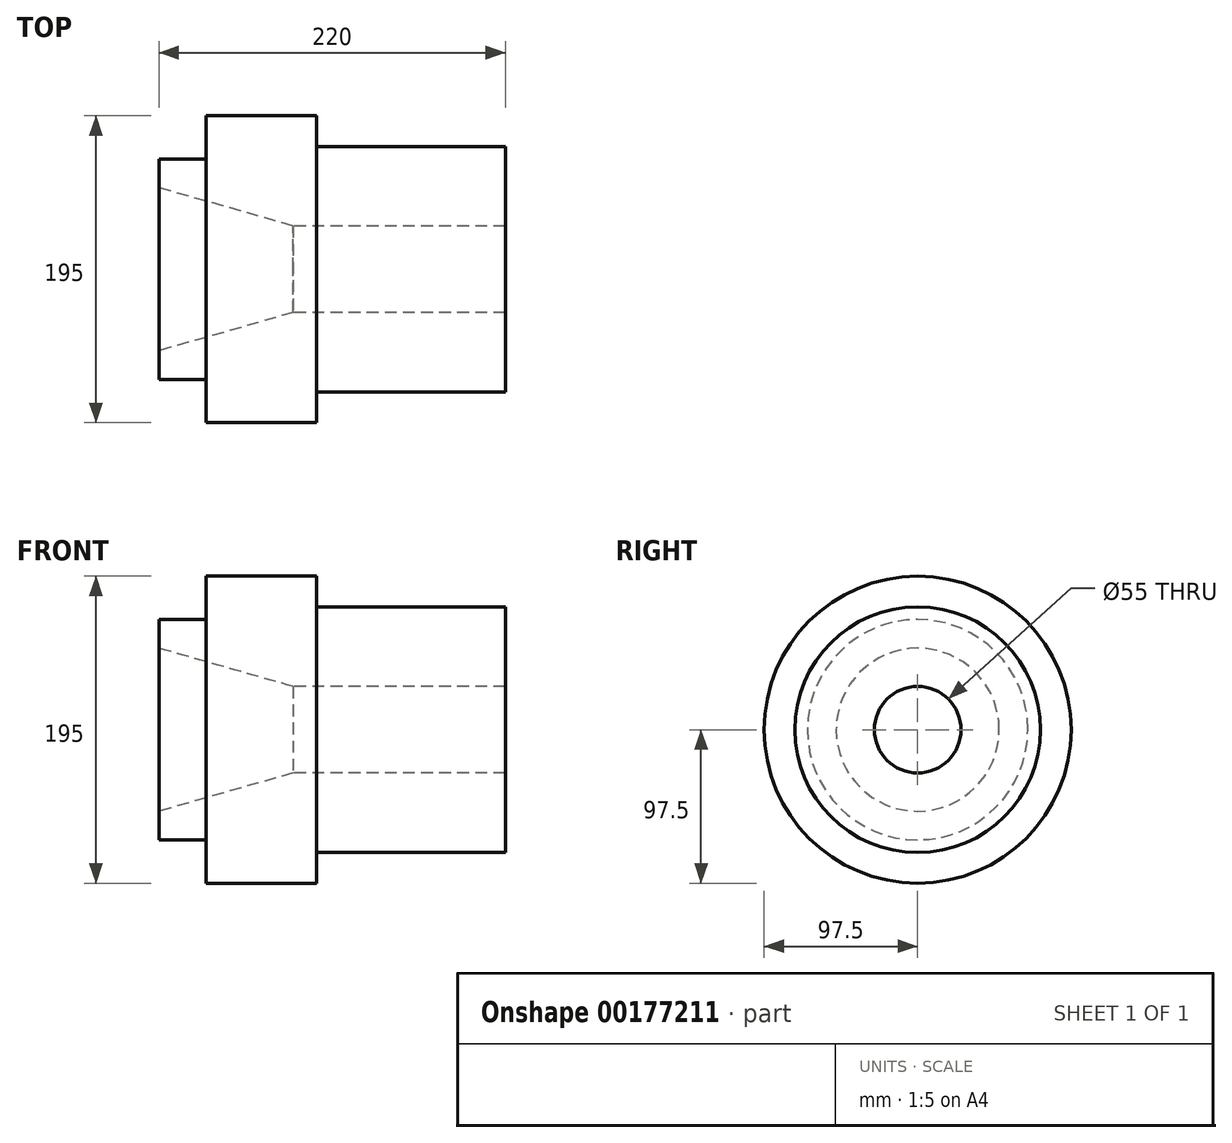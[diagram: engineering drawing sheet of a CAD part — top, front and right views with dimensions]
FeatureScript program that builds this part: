
annotation { "Feature Type Name" : "Feature", "Feature Type Description" : "" }
export const myFeature = defineFeature(function(context is Context, id is Id, definition is map)
    precondition{}
    {
        {
            var Q0;
            Q0=qCreatedBy(makeId("Front.planeOp"),FACE);
            var sketch = newSketch(context, id + "F0", { "sketchPlane" : qUnion([Q0])});
            skLineSegment(sketch, "E0", {"start": v(-95.27, 0) * mm, "end": v(96.4, 0) * mm, "construction": true});
            skLineSegment(sketch, "E1", {"start": v(120, 78) * mm, "end": v(120, 27.5) * mm});
            skLineSegment(sketch, "E2", {"start": v(120, 27.5) * mm, "end": v(-14.78, 27.5) * mm});
            skLineSegment(sketch, "E3", {"start": v(120, 78) * mm, "end": v(0, 78) * mm});
            skLineSegment(sketch, "E4", {"start": v(-14.78, 27.5) * mm, "end": v(-100, 51.78) * mm});
            skLineSegment(sketch, "E5", {"start": v(-100, 51.78) * mm, "end": v(-100, 70) * mm});
            skLineSegment(sketch, "E6", {"start": v(-100, 70) * mm, "end": v(-70, 70) * mm});
            skLineSegment(sketch, "E7", {"start": v(-70, 70) * mm, "end": v(-70, 97.5) * mm});
            skLineSegment(sketch, "E8", {"start": v(-70, 97.5) * mm, "end": v(0, 97.5) * mm});
            skLineSegment(sketch, "E9", {"start": v(0, 97.5) * mm, "end": v(0, 78) * mm});
            skSolve(sketch);
        }
        {
            var Q0;
            Q0=makeQuery(id+"F0.imprint","IMPRINT",FACE,{"disambiguationData":[TD([[makeQuery(id+"F0.imprint","IMPRINT",EDGE,{"derivedFrom":sQuery(id+"F0.wireOp",EDGE,"E1")}),-1.0]])]});
            var Q1;
            Q1=sQuery(id+"F0.wireOp",EDGE,"E0");
            revolve(context, id + "F1", {"entities" : qUnion([Q0]), "axis" : qUnion([Q1]), "revolveType" : RevolveType.FULL});
        }
    });
